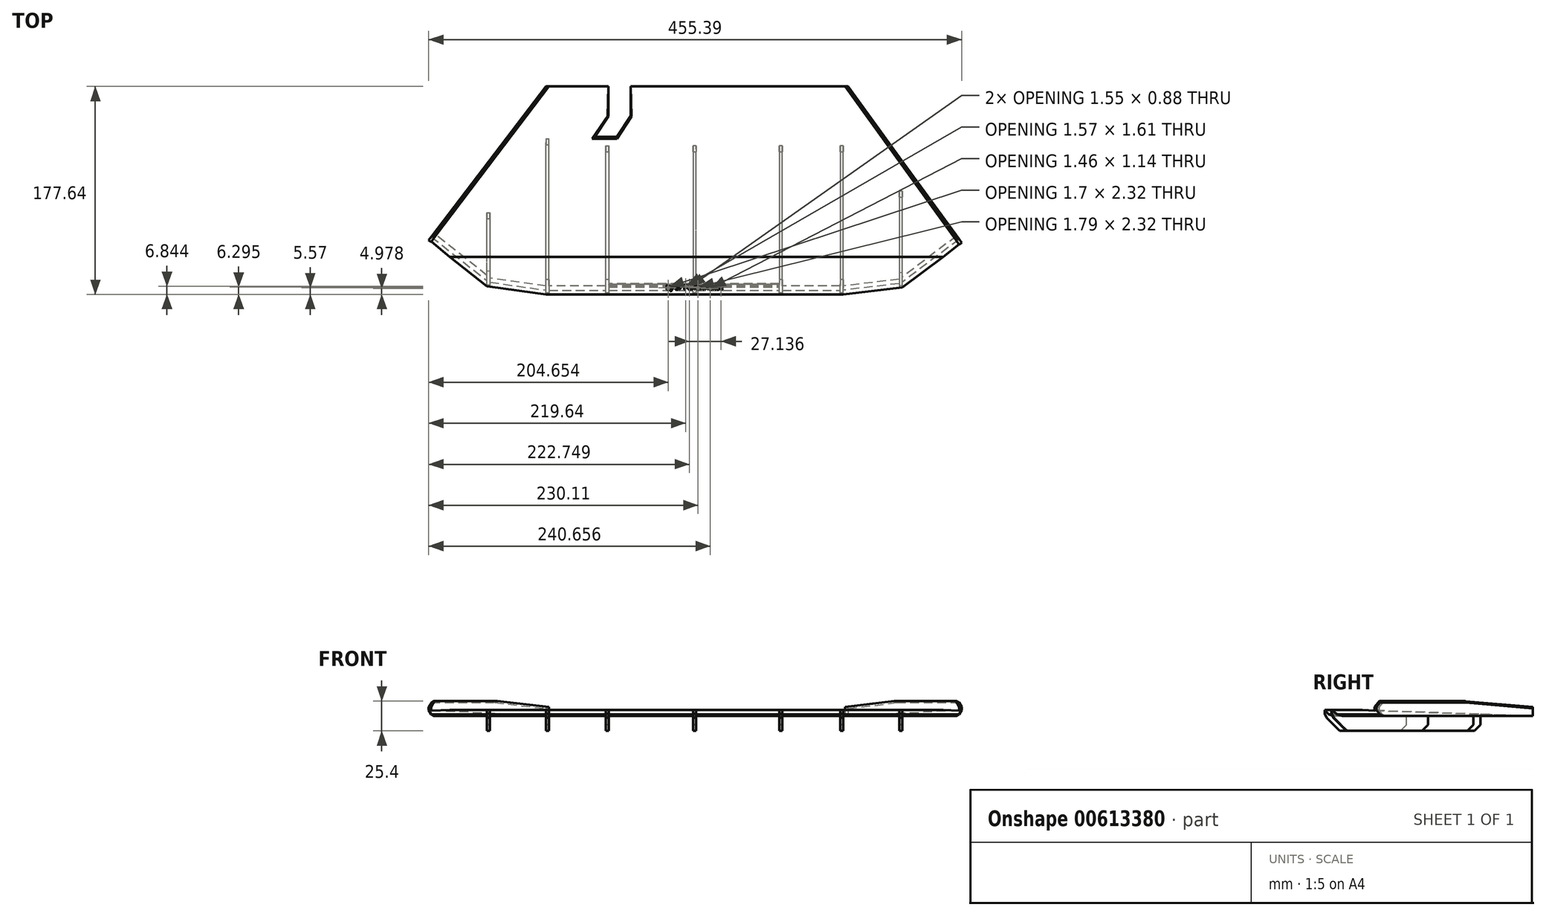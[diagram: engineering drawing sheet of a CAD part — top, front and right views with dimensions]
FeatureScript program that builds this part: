
annotation { "Feature Type Name" : "Feature", "Feature Type Description" : "" }
export const myFeature = defineFeature(function(context is Context, id is Id, definition is map)
    precondition{}
    {
        {
            var Q0;
            Q0=qCreatedBy(makeId("Top.planeOp"),FACE);
            var sketch = newSketch(context, id + "F0", { "sketchPlane" : qUnion([Q0])});
            skLineSegment(sketch, "E0.bottom", {"start": v(127, 146.68) * mm, "end": v(-127, 146.68) * mm});
            skLineSegment(sketch, "E0.top", {"start": v(127, 19.68) * mm, "end": v(-127, 19.68) * mm});
            skLineSegment(sketch, "E0.left", {"start": v(127, 146.68) * mm, "end": v(127, 19.68) * mm});
            skLineSegment(sketch, "E0.right", {"start": v(-127, 146.68) * mm, "end": v(-127, 19.68) * mm});
            skPoint(sketch, "E0.middle", {"position": v(0, 83.18) * mm});
            skLineSegment(sketch, "E1", {"start": v(-127, 146.68) * mm, "end": v(-127, 197.32) * mm});
            skLineSegment(sketch, "E2", {"start": v(-127, 197.32) * mm, "end": v(-73.7, 197.32) * mm});
            skLineSegment(sketch, "E3", {"start": v(-73.7, 197.32) * mm, "end": v(-73.7, 171.92) * mm});
            skLineSegment(sketch, "E4", {"start": v(-54.46, 171.92) * mm, "end": v(-54.46, 197.32) * mm});
            skLineSegment(sketch, "E5", {"start": v(-54.46, 197.32) * mm, "end": v(131.08, 197.32) * mm});
            skLineSegment(sketch, "E6", {"start": v(131.08, 197.32) * mm, "end": v(127, 146.68) * mm});
            skLineSegment(sketch, "E7", {"start": v(127, 19.68) * mm, "end": v(177.45, 25.67) * mm});
            skLineSegment(sketch, "E8", {"start": v(-127, 19.68) * mm, "end": v(-177.3, 26.78) * mm});
            skLineSegment(sketch, "E9", {"start": v(-177.3, 26.78) * mm, "end": v(-127, 197.32) * mm});
            skLineSegment(sketch, "E10", {"start": v(177.45, 25.67) * mm, "end": v(131.08, 197.32) * mm});
            skLineSegment(sketch, "E11", {"start": v(-73.7, 171.92) * mm, "end": v(-85.54, 154.36) * mm});
            skLineSegment(sketch, "E12", {"start": v(-85.54, 154.36) * mm, "end": v(-66.3, 154.36) * mm});
            skLineSegment(sketch, "E13", {"start": v(-66.3, 154.36) * mm, "end": v(-54.46, 171.92) * mm});
            skLineSegment(sketch, "E14", {"start": v(-177.3, 26.78) * mm, "end": v(-227.18, 66.08) * mm});
            skLineSegment(sketch, "E15", {"start": v(-227.18, 66.08) * mm, "end": v(-127, 197.32) * mm});
            skLineSegment(sketch, "E16", {"start": v(177.45, 25.67) * mm, "end": v(228.21, 63.82) * mm});
            skLineSegment(sketch, "E17", {"start": v(228.21, 63.82) * mm, "end": v(131.08, 197.32) * mm});
            skSolve(sketch);
        }
        {
            var Q0;
            Q0 = qSketchRegion(id + "F0", true);
            extrude(context, id + "F1", {"entities" : qUnion([Q0]), "depth" : 5.08 * mm, "offsetDistance" : 25.4 * mm});
        }
        {
            var Q0;
            Q0=makeQuery(id+"F1.opExtrude","CAP_FACE",FACE,{"disambiguationData":[OSD([sQuery(id+"F0.wireOp",EDGE,"E0.top"),sQuery(id+"F0.wireOp",EDGE,"E2"),sQuery(id+"F0.wireOp",EDGE,"E3"),sQuery(id+"F0.wireOp",EDGE,"E4"),sQuery(id+"F0.wireOp",EDGE,"E5"),sQuery(id+"F0.wireOp",EDGE,"E7"),sQuery(id+"F0.wireOp",EDGE,"E8"),sQuery(id+"F0.wireOp",EDGE,"E11"),sQuery(id+"F0.wireOp",EDGE,"E12"),sQuery(id+"F0.wireOp",EDGE,"E13"),sQuery(id+"F0.wireOp",EDGE,"E14"),sQuery(id+"F0.wireOp",EDGE,"E15"),sQuery(id+"F0.wireOp",EDGE,"E16"),sQuery(id+"F0.wireOp",EDGE,"E17")])],"isStart":false});
            var sketch = newSketch(context, id + "F2", { "sketchPlane" : qUnion([Q0])});
            skLineSegment(sketch, "E18", {"start": v(-227.18, 66.08) * mm, "end": v(-127, 197.32) * mm});
            skLineSegment(sketch, "E19", {"start": v(-227.18, 66.08) * mm, "end": v(-225.18, 64.51) * mm});
            skLineSegment(sketch, "E20", {"start": v(-124.46, 197.32) * mm, "end": v(-127, 197.32) * mm});
            skLineSegment(sketch, "E21", {"start": v(-225.18, 64.51) * mm, "end": v(-124.46, 197.32) * mm});
            skLineSegment(sketch, "E22", {"start": v(228.21, 63.82) * mm, "end": v(131.08, 197.32) * mm});
            skLineSegment(sketch, "E23", {"start": v(131.08, 197.32) * mm, "end": v(128.54, 197.32) * mm});
            skLineSegment(sketch, "E24", {"start": v(228.21, 63.82) * mm, "end": v(226.18, 62.29) * mm});
            skLineSegment(sketch, "E25", {"start": v(226.18, 62.29) * mm, "end": v(128.54, 197.32) * mm});
            skSolve(sketch);
        }
        {
            var Q0;
            Q0 = qSketchRegion(id + "F2", true);
            extrude(context, id + "F3", {"entities" : qUnion([Q0]), "operationType" : NewBodyOperationType.ADD, "depth" : 7.62 * mm, "offsetDistance" : 25.4 * mm});
        }
        {
            var Q0;
            Q0=makeQuery(id+"F1.opExtrude","CAP_FACE",FACE,{"disambiguationData":[OSD([sQuery(id+"F0.wireOp",EDGE,"E0.top"),sQuery(id+"F0.wireOp",EDGE,"E2"),sQuery(id+"F0.wireOp",EDGE,"E3"),sQuery(id+"F0.wireOp",EDGE,"E4"),sQuery(id+"F0.wireOp",EDGE,"E5"),sQuery(id+"F0.wireOp",EDGE,"E7"),sQuery(id+"F0.wireOp",EDGE,"E8"),sQuery(id+"F0.wireOp",EDGE,"E11"),sQuery(id+"F0.wireOp",EDGE,"E12"),sQuery(id+"F0.wireOp",EDGE,"E13"),sQuery(id+"F0.wireOp",EDGE,"E14"),sQuery(id+"F0.wireOp",EDGE,"E15"),sQuery(id+"F0.wireOp",EDGE,"E16"),sQuery(id+"F0.wireOp",EDGE,"E17")])],"isStart":true});
            var sketch = newSketch(context, id + "F4", { "sketchPlane" : qUnion([Q0])});
            skLineSegment(sketch, "E26", {"start": v(-127, -19.68) * mm, "end": v(-127, -152.72) * mm});
            skLineSegment(sketch, "E27", {"start": v(127, -19.68) * mm, "end": v(127, -146.68) * mm});
            skLineSegment(sketch, "E28", {"start": v(0, 0) * mm, "end": v(0, -146.68) * mm});
            skLineSegment(sketch, "E29", {"start": v(0, -146.68) * mm, "end": v(-1.27, -146.68) * mm});
            skLineSegment(sketch, "E30", {"start": v(0, -146.68) * mm, "end": v(1.27, -146.68) * mm});
            skLineSegment(sketch, "E31", {"start": v(-177.3, -26.78) * mm, "end": v(-177.3, -89.65) * mm});
            skLineSegment(sketch, "E32", {"start": v(177.45, -25.67) * mm, "end": v(177.45, -107.82) * mm});
            skLineSegment(sketch, "E33", {"start": v(-177.3, -26.78) * mm, "end": v(-174.79, -26.43) * mm});
            skLineSegment(sketch, "E34", {"start": v(-177.3, -89.65) * mm, "end": v(-174.76, -89.65) * mm});
            skLineSegment(sketch, "E35", {"start": v(-127, -19.68) * mm, "end": v(-124.46, -19.68) * mm});
            skLineSegment(sketch, "E36", {"start": v(-127, -152.72) * mm, "end": v(-124.46, -152.72) * mm});
            skLineSegment(sketch, "E37", {"start": v(0, -19.68) * mm, "end": v(-1.27, -19.68) * mm});
            skLineSegment(sketch, "E38", {"start": v(0, -19.68) * mm, "end": v(1.27, -19.68) * mm});
            skLineSegment(sketch, "E39", {"start": v(127, -19.68) * mm, "end": v(124.46, -19.68) * mm});
            skLineSegment(sketch, "E40", {"start": v(127, -146.68) * mm, "end": v(124.46, -146.68) * mm});
            skLineSegment(sketch, "E41", {"start": v(177.45, -25.67) * mm, "end": v(174.92, -25.37) * mm});
            skLineSegment(sketch, "E42", {"start": v(177.45, -107.82) * mm, "end": v(174.9, -107.82) * mm});
            skLineSegment(sketch, "E43", {"start": v(-174.76, -89.65) * mm, "end": v(-174.79, -26.43) * mm});
            skLineSegment(sketch, "E44", {"start": v(-124.46, -19.68) * mm, "end": v(-124.46, -152.72) * mm});
            skLineSegment(sketch, "E45", {"start": v(-1.27, -146.68) * mm, "end": v(-1.27, -19.68) * mm});
            skLineSegment(sketch, "E46", {"start": v(1.27, -19.68) * mm, "end": v(1.27, -146.68) * mm});
            skLineSegment(sketch, "E47", {"start": v(124.46, -146.68) * mm, "end": v(124.46, -19.68) * mm});
            skLineSegment(sketch, "E48", {"start": v(174.9, -107.82) * mm, "end": v(174.92, -25.37) * mm});
            skLineSegment(sketch, "E49", {"start": v(-75.92, -19.68) * mm, "end": v(-75.92, -146.68) * mm});
            skPoint(sketch, "E49.startSnap0", {"position": v(-75.92, -154.36) * mm});
            skLineSegment(sketch, "E50", {"start": v(74.96, -19.68) * mm, "end": v(74.96, -146.68) * mm});
            skLineSegment(sketch, "E51", {"start": v(74.96, -146.68) * mm, "end": v(72.42, -146.68) * mm});
            skLineSegment(sketch, "E52", {"start": v(74.96, -19.68) * mm, "end": v(72.42, -19.68) * mm});
            skLineSegment(sketch, "E53", {"start": v(-75.92, -19.68) * mm, "end": v(-73.38, -19.68) * mm});
            skLineSegment(sketch, "E54", {"start": v(-75.92, -146.68) * mm, "end": v(-73.38, -146.68) * mm});
            skLineSegment(sketch, "E55", {"start": v(-73.38, -146.68) * mm, "end": v(-73.38, -19.68) * mm});
            skLineSegment(sketch, "E56", {"start": v(72.42, -146.68) * mm, "end": v(72.42, -19.68) * mm});
            skSolve(sketch);
        }
        {
            var Q0;
            Q0 = qSketchRegion(id + "F4", true);
            extrude(context, id + "F5", {"entities" : qUnion([Q0]), "operationType" : NewBodyOperationType.ADD, "depth" : 12.7 * mm, "offsetDistance" : 25.4 * mm});
        }
        {
            var Q0;
            Q0=makeQuery(id+"F5.opExtrude","CAP_EDGE",EDGE,{"disambiguationData":[OSD([sQuery(id+"F4.wireOp",EDGE,"E33")])],"isStart":false});
            var Q1;
            Q1=makeQuery(id+"F5.opExtrude","CAP_EDGE",EDGE,{"disambiguationData":[OSD([sQuery(id+"F4.wireOp",EDGE,"E35")])],"isStart":false});
            var Q2;
            Q2=makeQuery(id+"F5.opExtrude","CAP_EDGE",EDGE,{"disambiguationData":[OSD([sQuery(id+"F4.wireOp",EDGE,"E53")])],"isStart":false});
            var Q3;
            Q3=makeQuery(id+"F5.opExtrude","CAP_EDGE",EDGE,{"disambiguationData":[OSD([sQuery(id+"F4.wireOp",EDGE,"E37"),sQuery(id+"F4.wireOp",EDGE,"E38")])],"isStart":false});
            var Q4;
            Q4=makeQuery(id+"F5.opExtrude","CAP_EDGE",EDGE,{"disambiguationData":[OSD([sQuery(id+"F4.wireOp",EDGE,"E52")])],"isStart":false});
            var Q5;
            Q5=makeQuery(id+"F5.opExtrude","CAP_EDGE",EDGE,{"disambiguationData":[OSD([sQuery(id+"F4.wireOp",EDGE,"E39")])],"isStart":false});
            var Q6;
            Q6=makeQuery(id+"F5.opExtrude","CAP_EDGE",EDGE,{"disambiguationData":[OSD([sQuery(id+"F4.wireOp",EDGE,"E41")])],"isStart":false});
            chamfer(context, id + "F6", {"entities" : qUnion([Q0, Q1, Q2, Q3, Q4, Q5, Q6]), "chamferType" : ChamferType.OFFSET_ANGLE, "width" : 12.7 * mm, "oppositeDirection" : false, "angle" : 45 * degree, "tangentPropagation" : true});
        }
        {
            var Q0;
            Q0=makeQuery(id+"F1.opExtrude","CAP_EDGE",EDGE,{"disambiguationData":[OSD([sQuery(id+"F0.wireOp",EDGE,"E14")])],"isStart":true});
            var Q1;
            Q1=makeQuery(id+"F1.opExtrude","CAP_EDGE",EDGE,{"disambiguationData":[OSD([sQuery(id+"F0.wireOp",EDGE,"E8")])],"isStart":true});
            var Q2;
            {var subQ0=sQuery(id+"F0.wireOp",EDGE,"E0.top");Q2=makeQuery(id+"F5.boolean.opBoolean","SPLIT",EDGE,{"disambiguationData":[TD([makeQuery(id+"F5.opExtrude","SWEPT_FACE",FACE,{"disambiguationData":[OSD([sQuery(id+"F4.wireOp",EDGE,"E44")])]})])],"derivedFrom":makeQuery(id+"F1.opExtrude","CAP_EDGE",EDGE,{"disambiguationData":[OSD([subQ0])],"isStart":true})});}
            var Q3;
            {var subQ0=sQuery(id+"F0.wireOp",EDGE,"E0.top");Q3=makeQuery(id+"F5.boolean.opBoolean","SPLIT",EDGE,{"disambiguationData":[TD([makeQuery(id+"F5.opExtrude","SWEPT_FACE",FACE,{"disambiguationData":[OSD([sQuery(id+"F4.wireOp",EDGE,"E45")])]})])],"derivedFrom":makeQuery(id+"F1.opExtrude","CAP_EDGE",EDGE,{"disambiguationData":[OSD([subQ0])],"isStart":true})});}
            var Q4;
            {var subQ0=sQuery(id+"F0.wireOp",EDGE,"E0.top");Q4=makeQuery(id+"F5.boolean.opBoolean","SPLIT",EDGE,{"disambiguationData":[TD([makeQuery(id+"F5.opExtrude","SWEPT_FACE",FACE,{"disambiguationData":[OSD([sQuery(id+"F4.wireOp",EDGE,"E46")])]})])],"derivedFrom":makeQuery(id+"F1.opExtrude","CAP_EDGE",EDGE,{"disambiguationData":[OSD([subQ0])],"isStart":true})});}
            var Q5;
            {var subQ0=sQuery(id+"F0.wireOp",EDGE,"E0.top");Q5=makeQuery(id+"F5.boolean.opBoolean","SPLIT",EDGE,{"disambiguationData":[TD([makeQuery(id+"F5.opExtrude","SWEPT_FACE",FACE,{"disambiguationData":[OSD([sQuery(id+"F4.wireOp",EDGE,"E47")])]})])],"derivedFrom":makeQuery(id+"F1.opExtrude","CAP_EDGE",EDGE,{"disambiguationData":[OSD([subQ0])],"isStart":true})});}
            var Q6;
            Q6=makeQuery(id+"F1.opExtrude","CAP_EDGE",EDGE,{"disambiguationData":[OSD([sQuery(id+"F0.wireOp",EDGE,"E7")])],"isStart":true});
            var Q7;
            Q7=makeQuery(id+"F1.opExtrude","CAP_EDGE",EDGE,{"disambiguationData":[OSD([sQuery(id+"F0.wireOp",EDGE,"E16")])],"isStart":true});
            chamfer(context, id + "F7", {"entities" : qUnion([Q0, Q1, Q2, Q3, Q4, Q5, Q6, Q7]), "width" : 5.08 * mm, "tangentPropagation" : true});
        }
        {
            var Q0;
            Q0=makeQuery(id+"F3.opExtrude","CAP_EDGE",EDGE,{"disambiguationData":[OSD([sQuery(id+"F2.wireOp",EDGE,"E23")])],"isStart":false});
            var Q1;
            Q1=makeQuery(id+"F3.opExtrude","CAP_EDGE",EDGE,{"disambiguationData":[OSD([sQuery(id+"F2.wireOp",EDGE,"E20")])],"isStart":false});
            chamfer(context, id + "F8", {"entities" : qUnion([Q0, Q1]), "chamferType" : ChamferType.OFFSET_ANGLE, "width" : 5.08 * mm, "oppositeDirection" : false, "angle" : 85 * degree, "tangentPropagation" : true});
        }
        {
            var Q0;
            Q0=makeQuery(id+"F3.opExtrude","CAP_EDGE",EDGE,{"disambiguationData":[OSD([sQuery(id+"F2.wireOp",EDGE,"E24")])],"isStart":false});
            var Q1;
            Q1=makeQuery(id+"F3.opExtrude","CAP_EDGE",EDGE,{"disambiguationData":[OSD([sQuery(id+"F2.wireOp",EDGE,"E19")])],"isStart":false});
            chamfer(context, id + "F9", {"entities" : qUnion([Q0, Q1]), "width" : 5.08 * mm, "tangentPropagation" : true});
        }
        {
            var Q0;
            {var subQ0=sQuery(id+"F4.wireOp",EDGE,"E53");Q0=makeQuery(id+"F6.opChamfer","BLEND_EDGE",EDGE,{"blendedFrom":[makeQuery(id+"F5.opExtrude","CAP_EDGE",EDGE,{"disambiguationData":[OSD([subQ0])],"isStart":false}),makeQuery(id+"F5.boolean.opBoolean","MERGE",FACE,{"derivedFrom":[makeQuery(id+"F1.opExtrude","SWEPT_FACE",FACE,{"disambiguationData":[OSD([sQuery(id+"F0.wireOp",EDGE,"E0.top")])]}),makeQuery(id+"F5.opExtrude","SWEPT_FACE",FACE,{"disambiguationData":[OSD([sQuery(id+"F4.wireOp",EDGE,"E35")])]}),makeQuery(id+"F5.opExtrude","SWEPT_FACE",FACE,{"disambiguationData":[OSD([sQuery(id+"F4.wireOp",EDGE,"E37"),sQuery(id+"F4.wireOp",EDGE,"E38")])]}),makeQuery(id+"F5.opExtrude","SWEPT_FACE",FACE,{"disambiguationData":[OSD([sQuery(id+"F4.wireOp",EDGE,"E39")])]}),makeQuery(id+"F5.opExtrude","SWEPT_FACE",FACE,{"disambiguationData":[OSD([sQuery(id+"F4.wireOp",EDGE,"E52")])]}),makeQuery(id+"F5.opExtrude","SWEPT_FACE",FACE,{"disambiguationData":[OSD([subQ0])]})]})],"blendedInto":[makeQuery(id+"F5.boolean.opBoolean","MERGE",FACE,{"derivedFrom":[makeQuery(id+"F1.opExtrude","SWEPT_FACE",FACE,{"disambiguationData":[OSD([sQuery(id+"F0.wireOp",EDGE,"E0.top")])]}),makeQuery(id+"F5.opExtrude","SWEPT_FACE",FACE,{"disambiguationData":[OSD([sQuery(id+"F4.wireOp",EDGE,"E35")])]}),makeQuery(id+"F5.opExtrude","SWEPT_FACE",FACE,{"disambiguationData":[OSD([sQuery(id+"F4.wireOp",EDGE,"E37"),sQuery(id+"F4.wireOp",EDGE,"E38")])]}),makeQuery(id+"F5.opExtrude","SWEPT_FACE",FACE,{"disambiguationData":[OSD([sQuery(id+"F4.wireOp",EDGE,"E39")])]}),makeQuery(id+"F5.opExtrude","SWEPT_FACE",FACE,{"disambiguationData":[OSD([sQuery(id+"F4.wireOp",EDGE,"E52")])]}),makeQuery(id+"F5.opExtrude","SWEPT_FACE",FACE,{"disambiguationData":[OSD([subQ0])]})]})]});}
            var Q1;
            {var subQ0=sQuery(id+"F4.wireOp",EDGE,"E38");var subQ1=sQuery(id+"F4.wireOp",EDGE,"E37");Q1=makeQuery(id+"F6.opChamfer","BLEND_EDGE",EDGE,{"blendedFrom":[makeQuery(id+"F5.opExtrude","CAP_EDGE",EDGE,{"disambiguationData":[OSD([subQ1,subQ0])],"isStart":false}),makeQuery(id+"F5.boolean.opBoolean","MERGE",FACE,{"derivedFrom":[makeQuery(id+"F1.opExtrude","SWEPT_FACE",FACE,{"disambiguationData":[OSD([sQuery(id+"F0.wireOp",EDGE,"E0.top")])]}),makeQuery(id+"F5.opExtrude","SWEPT_FACE",FACE,{"disambiguationData":[OSD([sQuery(id+"F4.wireOp",EDGE,"E35")])]}),makeQuery(id+"F5.opExtrude","SWEPT_FACE",FACE,{"disambiguationData":[OSD([subQ1,subQ0])]}),makeQuery(id+"F5.opExtrude","SWEPT_FACE",FACE,{"disambiguationData":[OSD([sQuery(id+"F4.wireOp",EDGE,"E39")])]}),makeQuery(id+"F5.opExtrude","SWEPT_FACE",FACE,{"disambiguationData":[OSD([sQuery(id+"F4.wireOp",EDGE,"E52")])]}),makeQuery(id+"F5.opExtrude","SWEPT_FACE",FACE,{"disambiguationData":[OSD([sQuery(id+"F4.wireOp",EDGE,"E53")])]})]})],"blendedInto":[makeQuery(id+"F5.boolean.opBoolean","MERGE",FACE,{"derivedFrom":[makeQuery(id+"F1.opExtrude","SWEPT_FACE",FACE,{"disambiguationData":[OSD([sQuery(id+"F0.wireOp",EDGE,"E0.top")])]}),makeQuery(id+"F5.opExtrude","SWEPT_FACE",FACE,{"disambiguationData":[OSD([sQuery(id+"F4.wireOp",EDGE,"E35")])]}),makeQuery(id+"F5.opExtrude","SWEPT_FACE",FACE,{"disambiguationData":[OSD([subQ1,subQ0])]}),makeQuery(id+"F5.opExtrude","SWEPT_FACE",FACE,{"disambiguationData":[OSD([sQuery(id+"F4.wireOp",EDGE,"E39")])]}),makeQuery(id+"F5.opExtrude","SWEPT_FACE",FACE,{"disambiguationData":[OSD([sQuery(id+"F4.wireOp",EDGE,"E52")])]}),makeQuery(id+"F5.opExtrude","SWEPT_FACE",FACE,{"disambiguationData":[OSD([sQuery(id+"F4.wireOp",EDGE,"E53")])]})]})]});}
            var Q2;
            {var subQ0=sQuery(id+"F4.wireOp",EDGE,"E52");Q2=makeQuery(id+"F6.opChamfer","BLEND_EDGE",EDGE,{"blendedFrom":[makeQuery(id+"F5.opExtrude","CAP_EDGE",EDGE,{"disambiguationData":[OSD([subQ0])],"isStart":false}),makeQuery(id+"F5.boolean.opBoolean","MERGE",FACE,{"derivedFrom":[makeQuery(id+"F1.opExtrude","SWEPT_FACE",FACE,{"disambiguationData":[OSD([sQuery(id+"F0.wireOp",EDGE,"E0.top")])]}),makeQuery(id+"F5.opExtrude","SWEPT_FACE",FACE,{"disambiguationData":[OSD([sQuery(id+"F4.wireOp",EDGE,"E35")])]}),makeQuery(id+"F5.opExtrude","SWEPT_FACE",FACE,{"disambiguationData":[OSD([sQuery(id+"F4.wireOp",EDGE,"E37"),sQuery(id+"F4.wireOp",EDGE,"E38")])]}),makeQuery(id+"F5.opExtrude","SWEPT_FACE",FACE,{"disambiguationData":[OSD([sQuery(id+"F4.wireOp",EDGE,"E39")])]}),makeQuery(id+"F5.opExtrude","SWEPT_FACE",FACE,{"disambiguationData":[OSD([subQ0])]}),makeQuery(id+"F5.opExtrude","SWEPT_FACE",FACE,{"disambiguationData":[OSD([sQuery(id+"F4.wireOp",EDGE,"E53")])]})]})],"blendedInto":[makeQuery(id+"F5.boolean.opBoolean","MERGE",FACE,{"derivedFrom":[makeQuery(id+"F1.opExtrude","SWEPT_FACE",FACE,{"disambiguationData":[OSD([sQuery(id+"F0.wireOp",EDGE,"E0.top")])]}),makeQuery(id+"F5.opExtrude","SWEPT_FACE",FACE,{"disambiguationData":[OSD([sQuery(id+"F4.wireOp",EDGE,"E35")])]}),makeQuery(id+"F5.opExtrude","SWEPT_FACE",FACE,{"disambiguationData":[OSD([sQuery(id+"F4.wireOp",EDGE,"E37"),sQuery(id+"F4.wireOp",EDGE,"E38")])]}),makeQuery(id+"F5.opExtrude","SWEPT_FACE",FACE,{"disambiguationData":[OSD([sQuery(id+"F4.wireOp",EDGE,"E39")])]}),makeQuery(id+"F5.opExtrude","SWEPT_FACE",FACE,{"disambiguationData":[OSD([subQ0])]}),makeQuery(id+"F5.opExtrude","SWEPT_FACE",FACE,{"disambiguationData":[OSD([sQuery(id+"F4.wireOp",EDGE,"E53")])]})]})]});}
            var Q3;
            {var subQ0=sQuery(id+"F4.wireOp",EDGE,"E39");Q3=makeQuery(id+"F6.opChamfer","BLEND_EDGE",EDGE,{"blendedFrom":[makeQuery(id+"F5.opExtrude","CAP_EDGE",EDGE,{"disambiguationData":[OSD([subQ0])],"isStart":false}),makeQuery(id+"F5.boolean.opBoolean","MERGE",FACE,{"derivedFrom":[makeQuery(id+"F1.opExtrude","SWEPT_FACE",FACE,{"disambiguationData":[OSD([sQuery(id+"F0.wireOp",EDGE,"E0.top")])]}),makeQuery(id+"F5.opExtrude","SWEPT_FACE",FACE,{"disambiguationData":[OSD([sQuery(id+"F4.wireOp",EDGE,"E35")])]}),makeQuery(id+"F5.opExtrude","SWEPT_FACE",FACE,{"disambiguationData":[OSD([sQuery(id+"F4.wireOp",EDGE,"E37"),sQuery(id+"F4.wireOp",EDGE,"E38")])]}),makeQuery(id+"F5.opExtrude","SWEPT_FACE",FACE,{"disambiguationData":[OSD([subQ0])]}),makeQuery(id+"F5.opExtrude","SWEPT_FACE",FACE,{"disambiguationData":[OSD([sQuery(id+"F4.wireOp",EDGE,"E52")])]}),makeQuery(id+"F5.opExtrude","SWEPT_FACE",FACE,{"disambiguationData":[OSD([sQuery(id+"F4.wireOp",EDGE,"E53")])]})]})],"blendedInto":[makeQuery(id+"F5.boolean.opBoolean","MERGE",FACE,{"derivedFrom":[makeQuery(id+"F1.opExtrude","SWEPT_FACE",FACE,{"disambiguationData":[OSD([sQuery(id+"F0.wireOp",EDGE,"E0.top")])]}),makeQuery(id+"F5.opExtrude","SWEPT_FACE",FACE,{"disambiguationData":[OSD([sQuery(id+"F4.wireOp",EDGE,"E35")])]}),makeQuery(id+"F5.opExtrude","SWEPT_FACE",FACE,{"disambiguationData":[OSD([sQuery(id+"F4.wireOp",EDGE,"E37"),sQuery(id+"F4.wireOp",EDGE,"E38")])]}),makeQuery(id+"F5.opExtrude","SWEPT_FACE",FACE,{"disambiguationData":[OSD([subQ0])]}),makeQuery(id+"F5.opExtrude","SWEPT_FACE",FACE,{"disambiguationData":[OSD([sQuery(id+"F4.wireOp",EDGE,"E52")])]}),makeQuery(id+"F5.opExtrude","SWEPT_FACE",FACE,{"disambiguationData":[OSD([sQuery(id+"F4.wireOp",EDGE,"E53")])]})]})]});}
            var Q4;
            {var subQ0=sQuery(id+"F4.wireOp",EDGE,"E41");Q4=makeQuery(id+"F6.opChamfer","BLEND_EDGE",EDGE,{"blendedFrom":[makeQuery(id+"F5.opExtrude","CAP_EDGE",EDGE,{"disambiguationData":[OSD([subQ0])],"isStart":false}),makeQuery(id+"F5.boolean.opBoolean","MERGE",FACE,{"derivedFrom":[makeQuery(id+"F1.opExtrude","SWEPT_FACE",FACE,{"disambiguationData":[OSD([sQuery(id+"F0.wireOp",EDGE,"E7")])]}),makeQuery(id+"F5.opExtrude","SWEPT_FACE",FACE,{"disambiguationData":[OSD([subQ0])]})]})],"blendedInto":[makeQuery(id+"F5.boolean.opBoolean","MERGE",FACE,{"derivedFrom":[makeQuery(id+"F1.opExtrude","SWEPT_FACE",FACE,{"disambiguationData":[OSD([sQuery(id+"F0.wireOp",EDGE,"E7")])]}),makeQuery(id+"F5.opExtrude","SWEPT_FACE",FACE,{"disambiguationData":[OSD([subQ0])]})]})]});}
            var Q5;
            {var subQ0=sQuery(id+"F4.wireOp",EDGE,"E33");Q5=makeQuery(id+"F6.opChamfer","BLEND_EDGE",EDGE,{"blendedFrom":[makeQuery(id+"F5.opExtrude","CAP_EDGE",EDGE,{"disambiguationData":[OSD([subQ0])],"isStart":false}),makeQuery(id+"F5.boolean.opBoolean","MERGE",FACE,{"derivedFrom":[makeQuery(id+"F1.opExtrude","SWEPT_FACE",FACE,{"disambiguationData":[OSD([sQuery(id+"F0.wireOp",EDGE,"E8")])]}),makeQuery(id+"F5.opExtrude","SWEPT_FACE",FACE,{"disambiguationData":[OSD([subQ0])]})]})],"blendedInto":[makeQuery(id+"F5.boolean.opBoolean","MERGE",FACE,{"derivedFrom":[makeQuery(id+"F1.opExtrude","SWEPT_FACE",FACE,{"disambiguationData":[OSD([sQuery(id+"F0.wireOp",EDGE,"E8")])]}),makeQuery(id+"F5.opExtrude","SWEPT_FACE",FACE,{"disambiguationData":[OSD([subQ0])]})]})]});}
            var Q6;
            {var subQ0=sQuery(id+"F4.wireOp",EDGE,"E35");Q6=makeQuery(id+"F6.opChamfer","BLEND_EDGE",EDGE,{"blendedFrom":[makeQuery(id+"F5.opExtrude","CAP_EDGE",EDGE,{"disambiguationData":[OSD([subQ0])],"isStart":false}),makeQuery(id+"F5.boolean.opBoolean","MERGE",FACE,{"derivedFrom":[makeQuery(id+"F1.opExtrude","SWEPT_FACE",FACE,{"disambiguationData":[OSD([sQuery(id+"F0.wireOp",EDGE,"E0.top")])]}),makeQuery(id+"F5.opExtrude","SWEPT_FACE",FACE,{"disambiguationData":[OSD([subQ0])]}),makeQuery(id+"F5.opExtrude","SWEPT_FACE",FACE,{"disambiguationData":[OSD([sQuery(id+"F4.wireOp",EDGE,"E37"),sQuery(id+"F4.wireOp",EDGE,"E38")])]}),makeQuery(id+"F5.opExtrude","SWEPT_FACE",FACE,{"disambiguationData":[OSD([sQuery(id+"F4.wireOp",EDGE,"E39")])]}),makeQuery(id+"F5.opExtrude","SWEPT_FACE",FACE,{"disambiguationData":[OSD([sQuery(id+"F4.wireOp",EDGE,"E52")])]}),makeQuery(id+"F5.opExtrude","SWEPT_FACE",FACE,{"disambiguationData":[OSD([sQuery(id+"F4.wireOp",EDGE,"E53")])]})]})],"blendedInto":[makeQuery(id+"F5.boolean.opBoolean","MERGE",FACE,{"derivedFrom":[makeQuery(id+"F1.opExtrude","SWEPT_FACE",FACE,{"disambiguationData":[OSD([sQuery(id+"F0.wireOp",EDGE,"E0.top")])]}),makeQuery(id+"F5.opExtrude","SWEPT_FACE",FACE,{"disambiguationData":[OSD([subQ0])]}),makeQuery(id+"F5.opExtrude","SWEPT_FACE",FACE,{"disambiguationData":[OSD([sQuery(id+"F4.wireOp",EDGE,"E37"),sQuery(id+"F4.wireOp",EDGE,"E38")])]}),makeQuery(id+"F5.opExtrude","SWEPT_FACE",FACE,{"disambiguationData":[OSD([sQuery(id+"F4.wireOp",EDGE,"E39")])]}),makeQuery(id+"F5.opExtrude","SWEPT_FACE",FACE,{"disambiguationData":[OSD([sQuery(id+"F4.wireOp",EDGE,"E52")])]}),makeQuery(id+"F5.opExtrude","SWEPT_FACE",FACE,{"disambiguationData":[OSD([sQuery(id+"F4.wireOp",EDGE,"E53")])]})]})]});}
            chamfer(context, id + "F10", {"entities" : qUnion([Q0, Q1, Q2, Q3, Q4, Q5, Q6]), "width" : 5.08 * mm, "tangentPropagation" : true});
        }
        {
            var Q0;
            {var subQ0=sQuery(id+"F0.wireOp",EDGE,"E0.top");var subQ1=makeQuery(id+"F1.opExtrude","CAP_FACE",FACE,{"disambiguationData":[OSD([subQ0,sQuery(id+"F0.wireOp",EDGE,"E2"),sQuery(id+"F0.wireOp",EDGE,"E3"),sQuery(id+"F0.wireOp",EDGE,"E4"),sQuery(id+"F0.wireOp",EDGE,"E5"),sQuery(id+"F0.wireOp",EDGE,"E7"),sQuery(id+"F0.wireOp",EDGE,"E8"),sQuery(id+"F0.wireOp",EDGE,"E11"),sQuery(id+"F0.wireOp",EDGE,"E12"),sQuery(id+"F0.wireOp",EDGE,"E13"),sQuery(id+"F0.wireOp",EDGE,"E14"),sQuery(id+"F0.wireOp",EDGE,"E15"),sQuery(id+"F0.wireOp",EDGE,"E16"),sQuery(id+"F0.wireOp",EDGE,"E17")])],"isStart":true});Q0=makeQuery(id+"F7.opChamfer","BLEND_EDGE",EDGE,{"blendedFrom":[makeQuery(id+"F5.boolean.opBoolean","SPLIT",EDGE,{"disambiguationData":[TD([makeQuery(id+"F5.opExtrude","SWEPT_FACE",FACE,{"disambiguationData":[OSD([sQuery(id+"F4.wireOp",EDGE,"E45")])]})])],"derivedFrom":makeQuery(id+"F1.opExtrude","CAP_EDGE",EDGE,{"disambiguationData":[OSD([subQ0])],"isStart":true})}),subQ1],"blendedInto":[subQ1]});}
            var Q1;
            {var subQ0=sQuery(id+"F0.wireOp",EDGE,"E0.top");var subQ1=makeQuery(id+"F1.opExtrude","CAP_FACE",FACE,{"disambiguationData":[OSD([subQ0,sQuery(id+"F0.wireOp",EDGE,"E2"),sQuery(id+"F0.wireOp",EDGE,"E3"),sQuery(id+"F0.wireOp",EDGE,"E4"),sQuery(id+"F0.wireOp",EDGE,"E5"),sQuery(id+"F0.wireOp",EDGE,"E7"),sQuery(id+"F0.wireOp",EDGE,"E8"),sQuery(id+"F0.wireOp",EDGE,"E11"),sQuery(id+"F0.wireOp",EDGE,"E12"),sQuery(id+"F0.wireOp",EDGE,"E13"),sQuery(id+"F0.wireOp",EDGE,"E14"),sQuery(id+"F0.wireOp",EDGE,"E15"),sQuery(id+"F0.wireOp",EDGE,"E16"),sQuery(id+"F0.wireOp",EDGE,"E17")])],"isStart":true});Q1=makeQuery(id+"F7.opChamfer","BLEND_EDGE",EDGE,{"blendedFrom":[makeQuery(id+"F5.boolean.opBoolean","SPLIT",EDGE,{"disambiguationData":[TD([makeQuery(id+"F5.opExtrude","SWEPT_FACE",FACE,{"disambiguationData":[OSD([sQuery(id+"F4.wireOp",EDGE,"E46")])]})])],"derivedFrom":makeQuery(id+"F1.opExtrude","CAP_EDGE",EDGE,{"disambiguationData":[OSD([subQ0])],"isStart":true})}),subQ1],"blendedInto":[subQ1]});}
            chamfer(context, id + "F11", {"entities" : qUnion([Q0, Q1]), "width" : 5.08 * mm, "tangentPropagation" : true});
        }
        {
            var Q0;
            {var subQ0=sQuery(id+"F0.wireOp",EDGE,"E0.top");var subQ1=makeQuery(id+"F1.opExtrude","CAP_FACE",FACE,{"disambiguationData":[OSD([subQ0,sQuery(id+"F0.wireOp",EDGE,"E2"),sQuery(id+"F0.wireOp",EDGE,"E3"),sQuery(id+"F0.wireOp",EDGE,"E4"),sQuery(id+"F0.wireOp",EDGE,"E5"),sQuery(id+"F0.wireOp",EDGE,"E7"),sQuery(id+"F0.wireOp",EDGE,"E8"),sQuery(id+"F0.wireOp",EDGE,"E11"),sQuery(id+"F0.wireOp",EDGE,"E12"),sQuery(id+"F0.wireOp",EDGE,"E13"),sQuery(id+"F0.wireOp",EDGE,"E14"),sQuery(id+"F0.wireOp",EDGE,"E15"),sQuery(id+"F0.wireOp",EDGE,"E16"),sQuery(id+"F0.wireOp",EDGE,"E17")])],"isStart":true});Q0=makeQuery(id+"F7.opChamfer","BLEND_EDGE",EDGE,{"blendedFrom":[makeQuery(id+"F5.boolean.opBoolean","SPLIT",EDGE,{"disambiguationData":[TD([makeQuery(id+"F5.opExtrude","SWEPT_FACE",FACE,{"disambiguationData":[OSD([sQuery(id+"F4.wireOp",EDGE,"E44")])]})])],"derivedFrom":makeQuery(id+"F1.opExtrude","CAP_EDGE",EDGE,{"disambiguationData":[OSD([subQ0])],"isStart":true})}),subQ1],"blendedInto":[subQ1]});}
            var Q1;
            {var subQ0=sQuery(id+"F0.wireOp",EDGE,"E8");Q1=makeQuery(id+"F7.opChamfer","BLEND_EDGE",EDGE,{"blendedFrom":[makeQuery(id+"F1.opExtrude","CAP_EDGE",EDGE,{"disambiguationData":[OSD([subQ0])],"isStart":true}),makeQuery(id+"F1.opExtrude","CAP_FACE",FACE,{"disambiguationData":[OSD([sQuery(id+"F0.wireOp",EDGE,"E0.top"),sQuery(id+"F0.wireOp",EDGE,"E2"),sQuery(id+"F0.wireOp",EDGE,"E3"),sQuery(id+"F0.wireOp",EDGE,"E4"),sQuery(id+"F0.wireOp",EDGE,"E5"),sQuery(id+"F0.wireOp",EDGE,"E7"),subQ0,sQuery(id+"F0.wireOp",EDGE,"E11"),sQuery(id+"F0.wireOp",EDGE,"E12"),sQuery(id+"F0.wireOp",EDGE,"E13"),sQuery(id+"F0.wireOp",EDGE,"E14"),sQuery(id+"F0.wireOp",EDGE,"E15"),sQuery(id+"F0.wireOp",EDGE,"E16"),sQuery(id+"F0.wireOp",EDGE,"E17")])],"isStart":true})],"blendedInto":[makeQuery(id+"F1.opExtrude","CAP_FACE",FACE,{"disambiguationData":[OSD([sQuery(id+"F0.wireOp",EDGE,"E0.top"),sQuery(id+"F0.wireOp",EDGE,"E2"),sQuery(id+"F0.wireOp",EDGE,"E3"),sQuery(id+"F0.wireOp",EDGE,"E4"),sQuery(id+"F0.wireOp",EDGE,"E5"),sQuery(id+"F0.wireOp",EDGE,"E7"),subQ0,sQuery(id+"F0.wireOp",EDGE,"E11"),sQuery(id+"F0.wireOp",EDGE,"E12"),sQuery(id+"F0.wireOp",EDGE,"E13"),sQuery(id+"F0.wireOp",EDGE,"E14"),sQuery(id+"F0.wireOp",EDGE,"E15"),sQuery(id+"F0.wireOp",EDGE,"E16"),sQuery(id+"F0.wireOp",EDGE,"E17")])],"isStart":true})]});}
            var Q2;
            {var subQ0=sQuery(id+"F0.wireOp",EDGE,"E14");Q2=makeQuery(id+"F7.opChamfer","BLEND_EDGE",EDGE,{"blendedFrom":[makeQuery(id+"F1.opExtrude","CAP_EDGE",EDGE,{"disambiguationData":[OSD([subQ0])],"isStart":true}),makeQuery(id+"F1.opExtrude","CAP_FACE",FACE,{"disambiguationData":[OSD([sQuery(id+"F0.wireOp",EDGE,"E0.top"),sQuery(id+"F0.wireOp",EDGE,"E2"),sQuery(id+"F0.wireOp",EDGE,"E3"),sQuery(id+"F0.wireOp",EDGE,"E4"),sQuery(id+"F0.wireOp",EDGE,"E5"),sQuery(id+"F0.wireOp",EDGE,"E7"),sQuery(id+"F0.wireOp",EDGE,"E8"),sQuery(id+"F0.wireOp",EDGE,"E11"),sQuery(id+"F0.wireOp",EDGE,"E12"),sQuery(id+"F0.wireOp",EDGE,"E13"),subQ0,sQuery(id+"F0.wireOp",EDGE,"E15"),sQuery(id+"F0.wireOp",EDGE,"E16"),sQuery(id+"F0.wireOp",EDGE,"E17")])],"isStart":true})],"blendedInto":[makeQuery(id+"F1.opExtrude","CAP_FACE",FACE,{"disambiguationData":[OSD([sQuery(id+"F0.wireOp",EDGE,"E0.top"),sQuery(id+"F0.wireOp",EDGE,"E2"),sQuery(id+"F0.wireOp",EDGE,"E3"),sQuery(id+"F0.wireOp",EDGE,"E4"),sQuery(id+"F0.wireOp",EDGE,"E5"),sQuery(id+"F0.wireOp",EDGE,"E7"),sQuery(id+"F0.wireOp",EDGE,"E8"),sQuery(id+"F0.wireOp",EDGE,"E11"),sQuery(id+"F0.wireOp",EDGE,"E12"),sQuery(id+"F0.wireOp",EDGE,"E13"),subQ0,sQuery(id+"F0.wireOp",EDGE,"E15"),sQuery(id+"F0.wireOp",EDGE,"E16"),sQuery(id+"F0.wireOp",EDGE,"E17")])],"isStart":true})]});}
            var Q3;
            {var subQ0=sQuery(id+"F0.wireOp",EDGE,"E0.top");var subQ1=makeQuery(id+"F1.opExtrude","CAP_FACE",FACE,{"disambiguationData":[OSD([subQ0,sQuery(id+"F0.wireOp",EDGE,"E2"),sQuery(id+"F0.wireOp",EDGE,"E3"),sQuery(id+"F0.wireOp",EDGE,"E4"),sQuery(id+"F0.wireOp",EDGE,"E5"),sQuery(id+"F0.wireOp",EDGE,"E7"),sQuery(id+"F0.wireOp",EDGE,"E8"),sQuery(id+"F0.wireOp",EDGE,"E11"),sQuery(id+"F0.wireOp",EDGE,"E12"),sQuery(id+"F0.wireOp",EDGE,"E13"),sQuery(id+"F0.wireOp",EDGE,"E14"),sQuery(id+"F0.wireOp",EDGE,"E15"),sQuery(id+"F0.wireOp",EDGE,"E16"),sQuery(id+"F0.wireOp",EDGE,"E17")])],"isStart":true});var subQ2=subQ1;Q3=makeQuery(id+"F11.opChamfer","BLEND_EDGE",EDGE,{"blendedFrom":[makeQuery(id+"F7.opChamfer","BLEND_EDGE",EDGE,{"blendedFrom":[makeQuery(id+"F5.boolean.opBoolean","SPLIT",EDGE,{"disambiguationData":[TD([makeQuery(id+"F5.opExtrude","SWEPT_FACE",FACE,{"disambiguationData":[OSD([sQuery(id+"F4.wireOp",EDGE,"E45")])]})])],"derivedFrom":makeQuery(id+"F1.opExtrude","CAP_EDGE",EDGE,{"disambiguationData":[OSD([subQ0])],"isStart":true})}),subQ2],"blendedInto":[subQ2]}),subQ2],"blendedInto":[subQ2]});}
            var Q4;
            {var subQ0=sQuery(id+"F0.wireOp",EDGE,"E0.top");var subQ1=makeQuery(id+"F1.opExtrude","CAP_FACE",FACE,{"disambiguationData":[OSD([subQ0,sQuery(id+"F0.wireOp",EDGE,"E2"),sQuery(id+"F0.wireOp",EDGE,"E3"),sQuery(id+"F0.wireOp",EDGE,"E4"),sQuery(id+"F0.wireOp",EDGE,"E5"),sQuery(id+"F0.wireOp",EDGE,"E7"),sQuery(id+"F0.wireOp",EDGE,"E8"),sQuery(id+"F0.wireOp",EDGE,"E11"),sQuery(id+"F0.wireOp",EDGE,"E12"),sQuery(id+"F0.wireOp",EDGE,"E13"),sQuery(id+"F0.wireOp",EDGE,"E14"),sQuery(id+"F0.wireOp",EDGE,"E15"),sQuery(id+"F0.wireOp",EDGE,"E16"),sQuery(id+"F0.wireOp",EDGE,"E17")])],"isStart":true});var subQ2=subQ1;Q4=makeQuery(id+"F11.opChamfer","BLEND_EDGE",EDGE,{"blendedFrom":[makeQuery(id+"F7.opChamfer","BLEND_EDGE",EDGE,{"blendedFrom":[makeQuery(id+"F5.boolean.opBoolean","SPLIT",EDGE,{"disambiguationData":[TD([makeQuery(id+"F5.opExtrude","SWEPT_FACE",FACE,{"disambiguationData":[OSD([sQuery(id+"F4.wireOp",EDGE,"E46")])]})])],"derivedFrom":makeQuery(id+"F1.opExtrude","CAP_EDGE",EDGE,{"disambiguationData":[OSD([subQ0])],"isStart":true})}),subQ2],"blendedInto":[subQ2]}),subQ2],"blendedInto":[subQ2]});}
            var Q5;
            {var subQ0=sQuery(id+"F0.wireOp",EDGE,"E0.top");var subQ1=makeQuery(id+"F1.opExtrude","CAP_FACE",FACE,{"disambiguationData":[OSD([subQ0,sQuery(id+"F0.wireOp",EDGE,"E2"),sQuery(id+"F0.wireOp",EDGE,"E3"),sQuery(id+"F0.wireOp",EDGE,"E4"),sQuery(id+"F0.wireOp",EDGE,"E5"),sQuery(id+"F0.wireOp",EDGE,"E7"),sQuery(id+"F0.wireOp",EDGE,"E8"),sQuery(id+"F0.wireOp",EDGE,"E11"),sQuery(id+"F0.wireOp",EDGE,"E12"),sQuery(id+"F0.wireOp",EDGE,"E13"),sQuery(id+"F0.wireOp",EDGE,"E14"),sQuery(id+"F0.wireOp",EDGE,"E15"),sQuery(id+"F0.wireOp",EDGE,"E16"),sQuery(id+"F0.wireOp",EDGE,"E17")])],"isStart":true});Q5=makeQuery(id+"F7.opChamfer","BLEND_EDGE",EDGE,{"blendedFrom":[makeQuery(id+"F5.boolean.opBoolean","SPLIT",EDGE,{"disambiguationData":[TD([makeQuery(id+"F5.opExtrude","SWEPT_FACE",FACE,{"disambiguationData":[OSD([sQuery(id+"F4.wireOp",EDGE,"E47")])]})])],"derivedFrom":makeQuery(id+"F1.opExtrude","CAP_EDGE",EDGE,{"disambiguationData":[OSD([subQ0])],"isStart":true})}),subQ1],"blendedInto":[subQ1]});}
            var Q6;
            {var subQ0=sQuery(id+"F0.wireOp",EDGE,"E7");Q6=makeQuery(id+"F7.opChamfer","BLEND_EDGE",EDGE,{"blendedFrom":[makeQuery(id+"F1.opExtrude","CAP_EDGE",EDGE,{"disambiguationData":[OSD([subQ0])],"isStart":true}),makeQuery(id+"F1.opExtrude","CAP_FACE",FACE,{"disambiguationData":[OSD([sQuery(id+"F0.wireOp",EDGE,"E0.top"),sQuery(id+"F0.wireOp",EDGE,"E2"),sQuery(id+"F0.wireOp",EDGE,"E3"),sQuery(id+"F0.wireOp",EDGE,"E4"),sQuery(id+"F0.wireOp",EDGE,"E5"),subQ0,sQuery(id+"F0.wireOp",EDGE,"E8"),sQuery(id+"F0.wireOp",EDGE,"E11"),sQuery(id+"F0.wireOp",EDGE,"E12"),sQuery(id+"F0.wireOp",EDGE,"E13"),sQuery(id+"F0.wireOp",EDGE,"E14"),sQuery(id+"F0.wireOp",EDGE,"E15"),sQuery(id+"F0.wireOp",EDGE,"E16"),sQuery(id+"F0.wireOp",EDGE,"E17")])],"isStart":true})],"blendedInto":[makeQuery(id+"F1.opExtrude","CAP_FACE",FACE,{"disambiguationData":[OSD([sQuery(id+"F0.wireOp",EDGE,"E0.top"),sQuery(id+"F0.wireOp",EDGE,"E2"),sQuery(id+"F0.wireOp",EDGE,"E3"),sQuery(id+"F0.wireOp",EDGE,"E4"),sQuery(id+"F0.wireOp",EDGE,"E5"),subQ0,sQuery(id+"F0.wireOp",EDGE,"E8"),sQuery(id+"F0.wireOp",EDGE,"E11"),sQuery(id+"F0.wireOp",EDGE,"E12"),sQuery(id+"F0.wireOp",EDGE,"E13"),sQuery(id+"F0.wireOp",EDGE,"E14"),sQuery(id+"F0.wireOp",EDGE,"E15"),sQuery(id+"F0.wireOp",EDGE,"E16"),sQuery(id+"F0.wireOp",EDGE,"E17")])],"isStart":true})]});}
            var Q7;
            {var subQ0=sQuery(id+"F0.wireOp",EDGE,"E16");Q7=makeQuery(id+"F7.opChamfer","BLEND_EDGE",EDGE,{"blendedFrom":[makeQuery(id+"F1.opExtrude","CAP_EDGE",EDGE,{"disambiguationData":[OSD([subQ0])],"isStart":true}),makeQuery(id+"F1.opExtrude","CAP_FACE",FACE,{"disambiguationData":[OSD([sQuery(id+"F0.wireOp",EDGE,"E0.top"),sQuery(id+"F0.wireOp",EDGE,"E2"),sQuery(id+"F0.wireOp",EDGE,"E3"),sQuery(id+"F0.wireOp",EDGE,"E4"),sQuery(id+"F0.wireOp",EDGE,"E5"),sQuery(id+"F0.wireOp",EDGE,"E7"),sQuery(id+"F0.wireOp",EDGE,"E8"),sQuery(id+"F0.wireOp",EDGE,"E11"),sQuery(id+"F0.wireOp",EDGE,"E12"),sQuery(id+"F0.wireOp",EDGE,"E13"),sQuery(id+"F0.wireOp",EDGE,"E14"),sQuery(id+"F0.wireOp",EDGE,"E15"),subQ0,sQuery(id+"F0.wireOp",EDGE,"E17")])],"isStart":true})],"blendedInto":[makeQuery(id+"F1.opExtrude","CAP_FACE",FACE,{"disambiguationData":[OSD([sQuery(id+"F0.wireOp",EDGE,"E0.top"),sQuery(id+"F0.wireOp",EDGE,"E2"),sQuery(id+"F0.wireOp",EDGE,"E3"),sQuery(id+"F0.wireOp",EDGE,"E4"),sQuery(id+"F0.wireOp",EDGE,"E5"),sQuery(id+"F0.wireOp",EDGE,"E7"),sQuery(id+"F0.wireOp",EDGE,"E8"),sQuery(id+"F0.wireOp",EDGE,"E11"),sQuery(id+"F0.wireOp",EDGE,"E12"),sQuery(id+"F0.wireOp",EDGE,"E13"),sQuery(id+"F0.wireOp",EDGE,"E14"),sQuery(id+"F0.wireOp",EDGE,"E15"),subQ0,sQuery(id+"F0.wireOp",EDGE,"E17")])],"isStart":true})]});}
            chamfer(context, id + "F12", {"entities" : qUnion([Q0, Q1, Q2, Q3, Q4, Q5, Q6, Q7]), "width" : 5.08 * mm, "tangentPropagation" : true});
        }
        {
            var Q0;
            Q0=makeQuery(id+"F1.opExtrude","CAP_FACE",FACE,{"disambiguationData":[OSD([sQuery(id+"F0.wireOp",EDGE,"E0.top"),sQuery(id+"F0.wireOp",EDGE,"E2"),sQuery(id+"F0.wireOp",EDGE,"E3"),sQuery(id+"F0.wireOp",EDGE,"E4"),sQuery(id+"F0.wireOp",EDGE,"E5"),sQuery(id+"F0.wireOp",EDGE,"E7"),sQuery(id+"F0.wireOp",EDGE,"E8"),sQuery(id+"F0.wireOp",EDGE,"E11"),sQuery(id+"F0.wireOp",EDGE,"E12"),sQuery(id+"F0.wireOp",EDGE,"E13"),sQuery(id+"F0.wireOp",EDGE,"E14"),sQuery(id+"F0.wireOp",EDGE,"E15"),sQuery(id+"F0.wireOp",EDGE,"E16"),sQuery(id+"F0.wireOp",EDGE,"E17")])],"isStart":false});
            var sketch = newSketch(context, id + "F13", { "sketchPlane" : qUnion([Q0])});
            skText(sketch, "E57", { "text": "by SF Performance", "fontName": "OpenSans-Regular.ttf"});
            const initialGuessF13  = {"E57": [-0.0243, 0.02377, 1, 0, 0.00399]};
            skSetInitialGuess(sketch, initialGuessF13);
            skSolve(sketch);
        }
        {
            var Q0;
            Q0 = qSketchRegion(id + "F13", true);
            extrude(context, id + "F14", {"entities" : qUnion([Q0]), "depth" : 0.03 * mm, "offsetDistance" : 25.4 * mm});
        }
        {
            var Q0;
            Q0=makeQuery(id+"F1.opExtrude","CAP_EDGE",EDGE,{"disambiguationData":[OSD([sQuery(id+"F0.wireOp",EDGE,"E12")])],"isStart":false});
            chamfer(context, id + "F15", {"entities" : qUnion([Q0]), "width" : 5.08 * mm, "tangentPropagation" : true});
        }
        {
            var Q0;
            Q0=makeQuery(id+"F1.opExtrude","CAP_EDGE",EDGE,{"disambiguationData":[OSD([sQuery(id+"F0.wireOp",EDGE,"E13")])],"isStart":false});
            var Q1;
            Q1=makeQuery(id+"F1.opExtrude","CAP_EDGE",EDGE,{"disambiguationData":[OSD([sQuery(id+"F0.wireOp",EDGE,"E4")])],"isStart":false});
            var Q2;
            Q2=makeQuery(id+"F1.opExtrude","CAP_EDGE",EDGE,{"disambiguationData":[OSD([sQuery(id+"F0.wireOp",EDGE,"E3")])],"isStart":false});
            var Q3;
            Q3=makeQuery(id+"F1.opExtrude","CAP_EDGE",EDGE,{"disambiguationData":[OSD([sQuery(id+"F0.wireOp",EDGE,"E11")])],"isStart":false});
            chamfer(context, id + "F16", {"entities" : qUnion([Q0, Q1, Q2, Q3]), "chamferType" : ChamferType.OFFSET_ANGLE, "width" : 5.08 * mm, "oppositeDirection" : false, "angle" : 30 * degree, "tangentPropagation" : true});
        }
        {
            var Q0;
            Q0=makeQuery(id+"F5.opExtrude","CAP_EDGE",EDGE,{"disambiguationData":[OSD([sQuery(id+"F4.wireOp",EDGE,"E34")])],"isStart":false});
            var Q1;
            Q1=makeQuery(id+"F5.opExtrude","CAP_EDGE",EDGE,{"disambiguationData":[OSD([sQuery(id+"F4.wireOp",EDGE,"E36")])],"isStart":false});
            var Q2;
            Q2=makeQuery(id+"F5.opExtrude","CAP_EDGE",EDGE,{"disambiguationData":[OSD([sQuery(id+"F4.wireOp",EDGE,"E54")])],"isStart":false});
            var Q3;
            Q3=makeQuery(id+"F5.opExtrude","CAP_EDGE",EDGE,{"disambiguationData":[OSD([sQuery(id+"F4.wireOp",EDGE,"E29"),sQuery(id+"F4.wireOp",EDGE,"E30")])],"isStart":false});
            var Q4;
            Q4=makeQuery(id+"F5.opExtrude","CAP_EDGE",EDGE,{"disambiguationData":[OSD([sQuery(id+"F4.wireOp",EDGE,"E51")])],"isStart":false});
            var Q5;
            Q5=makeQuery(id+"F5.opExtrude","CAP_EDGE",EDGE,{"disambiguationData":[OSD([sQuery(id+"F4.wireOp",EDGE,"E40")])],"isStart":false});
            var Q6;
            Q6=makeQuery(id+"F5.opExtrude","CAP_EDGE",EDGE,{"disambiguationData":[OSD([sQuery(id+"F4.wireOp",EDGE,"E42")])],"isStart":false});
            chamfer(context, id + "F17", {"entities" : qUnion([Q0, Q1, Q2, Q3, Q4, Q5, Q6]), "width" : 5.08 * mm, "tangentPropagation" : true});
        }
        {
            var Q0;
            Q0=makeQuery(id+"F1.opExtrude","CAP_EDGE",EDGE,{"disambiguationData":[OSD([sQuery(id+"F0.wireOp",EDGE,"E5")])],"isStart":false});
            chamfer(context, id + "F18", {"entities" : qUnion([Q0]), "chamferType" : ChamferType.OFFSET_ANGLE, "width" : 5.08 * mm, "oppositeDirection" : false, "angle" : 88 * degree, "tangentPropagation" : true});
        }
        {
            var Q0;
            Q0=makeQuery(id+"F3.opExtrude","CAP_EDGE",EDGE,{"disambiguationData":[OSD([sQuery(id+"F2.wireOp",EDGE,"E18")])],"isStart":false});
            var Q1;
            Q1=makeQuery(id+"F8.opChamfer","BLEND_EDGE",EDGE,{"blendedFrom":[makeQuery(id+"F3.opExtrude","CAP_EDGE",EDGE,{"disambiguationData":[OSD([sQuery(id+"F2.wireOp",EDGE,"E20")])],"isStart":false}),makeQuery(id+"F3.boolean.opBoolean","MERGE",FACE,{"derivedFrom":[makeQuery(id+"F1.opExtrude","SWEPT_FACE",FACE,{"disambiguationData":[OSD([sQuery(id+"F0.wireOp",EDGE,"E15")])]}),makeQuery(id+"F3.opExtrude","SWEPT_FACE",FACE,{"disambiguationData":[OSD([sQuery(id+"F2.wireOp",EDGE,"E18")])]})]})],"blendedInto":[makeQuery(id+"F3.boolean.opBoolean","MERGE",FACE,{"derivedFrom":[makeQuery(id+"F1.opExtrude","SWEPT_FACE",FACE,{"disambiguationData":[OSD([sQuery(id+"F0.wireOp",EDGE,"E15")])]}),makeQuery(id+"F3.opExtrude","SWEPT_FACE",FACE,{"disambiguationData":[OSD([sQuery(id+"F2.wireOp",EDGE,"E18")])]})]})]});
            var Q2;
            Q2=makeQuery(id+"F3.opExtrude","CAP_EDGE",EDGE,{"disambiguationData":[OSD([sQuery(id+"F2.wireOp",EDGE,"E22")])],"isStart":false});
            var Q3;
            Q3=makeQuery(id+"F8.opChamfer","BLEND_EDGE",EDGE,{"blendedFrom":[makeQuery(id+"F3.opExtrude","CAP_EDGE",EDGE,{"disambiguationData":[OSD([sQuery(id+"F2.wireOp",EDGE,"E23")])],"isStart":false}),makeQuery(id+"F3.boolean.opBoolean","MERGE",FACE,{"derivedFrom":[makeQuery(id+"F1.opExtrude","SWEPT_FACE",FACE,{"disambiguationData":[OSD([sQuery(id+"F0.wireOp",EDGE,"E17")])]}),makeQuery(id+"F3.opExtrude","SWEPT_FACE",FACE,{"disambiguationData":[OSD([sQuery(id+"F2.wireOp",EDGE,"E22")])]})]})],"blendedInto":[makeQuery(id+"F3.boolean.opBoolean","MERGE",FACE,{"derivedFrom":[makeQuery(id+"F1.opExtrude","SWEPT_FACE",FACE,{"disambiguationData":[OSD([sQuery(id+"F0.wireOp",EDGE,"E17")])]}),makeQuery(id+"F3.opExtrude","SWEPT_FACE",FACE,{"disambiguationData":[OSD([sQuery(id+"F2.wireOp",EDGE,"E22")])]})]})]});
            chamfer(context, id + "F19", {"entities" : qUnion([Q0, Q1, Q2, Q3]), "width" : 1.27 * mm, "tangentPropagation" : true});
        }
        {
            var Q0;
            {var subQ0=sQuery(id+"F0.wireOp",EDGE,"E0.top");var subQ1=makeQuery(id+"F1.opExtrude","CAP_FACE",FACE,{"disambiguationData":[OSD([subQ0,sQuery(id+"F0.wireOp",EDGE,"E2"),sQuery(id+"F0.wireOp",EDGE,"E3"),sQuery(id+"F0.wireOp",EDGE,"E4"),sQuery(id+"F0.wireOp",EDGE,"E5"),sQuery(id+"F0.wireOp",EDGE,"E7"),sQuery(id+"F0.wireOp",EDGE,"E8"),sQuery(id+"F0.wireOp",EDGE,"E11"),sQuery(id+"F0.wireOp",EDGE,"E12"),sQuery(id+"F0.wireOp",EDGE,"E13"),sQuery(id+"F0.wireOp",EDGE,"E14"),sQuery(id+"F0.wireOp",EDGE,"E15"),sQuery(id+"F0.wireOp",EDGE,"E16"),sQuery(id+"F0.wireOp",EDGE,"E17")])],"isStart":true});var subQ2=subQ1;var subQ3=subQ2;Q0=makeQuery(id+"F12.opChamfer","BLEND_EDGE",EDGE,{"blendedFrom":[makeQuery(id+"F11.opChamfer","BLEND_EDGE",EDGE,{"blendedFrom":[makeQuery(id+"F7.opChamfer","BLEND_EDGE",EDGE,{"blendedFrom":[makeQuery(id+"F5.boolean.opBoolean","SPLIT",EDGE,{"disambiguationData":[TD([makeQuery(id+"F5.opExtrude","SWEPT_FACE",FACE,{"disambiguationData":[OSD([sQuery(id+"F4.wireOp",EDGE,"E45")])]})])],"derivedFrom":makeQuery(id+"F1.opExtrude","CAP_EDGE",EDGE,{"disambiguationData":[OSD([subQ0])],"isStart":true})}),subQ2],"blendedInto":[subQ2]}),subQ3],"blendedInto":[subQ3]}),subQ3],"blendedInto":[subQ3]});}
            var Q1;
            {var subQ0=sQuery(id+"F0.wireOp",EDGE,"E0.top");var subQ1=makeQuery(id+"F1.opExtrude","CAP_FACE",FACE,{"disambiguationData":[OSD([subQ0,sQuery(id+"F0.wireOp",EDGE,"E2"),sQuery(id+"F0.wireOp",EDGE,"E3"),sQuery(id+"F0.wireOp",EDGE,"E4"),sQuery(id+"F0.wireOp",EDGE,"E5"),sQuery(id+"F0.wireOp",EDGE,"E7"),sQuery(id+"F0.wireOp",EDGE,"E8"),sQuery(id+"F0.wireOp",EDGE,"E11"),sQuery(id+"F0.wireOp",EDGE,"E12"),sQuery(id+"F0.wireOp",EDGE,"E13"),sQuery(id+"F0.wireOp",EDGE,"E14"),sQuery(id+"F0.wireOp",EDGE,"E15"),sQuery(id+"F0.wireOp",EDGE,"E16"),sQuery(id+"F0.wireOp",EDGE,"E17")])],"isStart":true});var subQ2=subQ1;var subQ3=subQ2;Q1=makeQuery(id+"F12.opChamfer","BLEND_EDGE",EDGE,{"blendedFrom":[makeQuery(id+"F11.opChamfer","BLEND_EDGE",EDGE,{"blendedFrom":[makeQuery(id+"F7.opChamfer","BLEND_EDGE",EDGE,{"blendedFrom":[makeQuery(id+"F5.boolean.opBoolean","SPLIT",EDGE,{"disambiguationData":[TD([makeQuery(id+"F5.opExtrude","SWEPT_FACE",FACE,{"disambiguationData":[OSD([sQuery(id+"F4.wireOp",EDGE,"E46")])]})])],"derivedFrom":makeQuery(id+"F1.opExtrude","CAP_EDGE",EDGE,{"disambiguationData":[OSD([subQ0])],"isStart":true})}),subQ2],"blendedInto":[subQ2]}),subQ3],"blendedInto":[subQ3]}),subQ3],"blendedInto":[subQ3]});}
            chamfer(context, id + "F20", {"entities" : qUnion([Q0, Q1]), "width" : 5.08 * mm, "tangentPropagation" : true});
        }
        {
            var Q0;
            {var subQ0=sQuery(id+"F0.wireOp",EDGE,"E0.top");var subQ1=makeQuery(id+"F1.opExtrude","CAP_FACE",FACE,{"disambiguationData":[OSD([subQ0,sQuery(id+"F0.wireOp",EDGE,"E2"),sQuery(id+"F0.wireOp",EDGE,"E3"),sQuery(id+"F0.wireOp",EDGE,"E4"),sQuery(id+"F0.wireOp",EDGE,"E5"),sQuery(id+"F0.wireOp",EDGE,"E7"),sQuery(id+"F0.wireOp",EDGE,"E8"),sQuery(id+"F0.wireOp",EDGE,"E11"),sQuery(id+"F0.wireOp",EDGE,"E12"),sQuery(id+"F0.wireOp",EDGE,"E13"),sQuery(id+"F0.wireOp",EDGE,"E14"),sQuery(id+"F0.wireOp",EDGE,"E15"),sQuery(id+"F0.wireOp",EDGE,"E16"),sQuery(id+"F0.wireOp",EDGE,"E17")])],"isStart":true});var subQ2=subQ1;var subQ3=subQ2;var subQ4=subQ3;Q0=makeQuery(id+"F20.opChamfer","BLEND_EDGE",EDGE,{"blendedFrom":[makeQuery(id+"F12.opChamfer","BLEND_EDGE",EDGE,{"blendedFrom":[makeQuery(id+"F11.opChamfer","BLEND_EDGE",EDGE,{"blendedFrom":[makeQuery(id+"F7.opChamfer","BLEND_EDGE",EDGE,{"blendedFrom":[makeQuery(id+"F5.boolean.opBoolean","SPLIT",EDGE,{"disambiguationData":[TD([makeQuery(id+"F5.opExtrude","SWEPT_FACE",FACE,{"disambiguationData":[OSD([sQuery(id+"F4.wireOp",EDGE,"E45")])]})])],"derivedFrom":makeQuery(id+"F1.opExtrude","CAP_EDGE",EDGE,{"disambiguationData":[OSD([subQ0])],"isStart":true})}),subQ2],"blendedInto":[subQ2]}),subQ3],"blendedInto":[subQ3]}),subQ4],"blendedInto":[subQ4]}),subQ4],"blendedInto":[subQ4]});}
            var Q1;
            {var subQ0=sQuery(id+"F0.wireOp",EDGE,"E0.top");var subQ1=makeQuery(id+"F1.opExtrude","CAP_FACE",FACE,{"disambiguationData":[OSD([subQ0,sQuery(id+"F0.wireOp",EDGE,"E2"),sQuery(id+"F0.wireOp",EDGE,"E3"),sQuery(id+"F0.wireOp",EDGE,"E4"),sQuery(id+"F0.wireOp",EDGE,"E5"),sQuery(id+"F0.wireOp",EDGE,"E7"),sQuery(id+"F0.wireOp",EDGE,"E8"),sQuery(id+"F0.wireOp",EDGE,"E11"),sQuery(id+"F0.wireOp",EDGE,"E12"),sQuery(id+"F0.wireOp",EDGE,"E13"),sQuery(id+"F0.wireOp",EDGE,"E14"),sQuery(id+"F0.wireOp",EDGE,"E15"),sQuery(id+"F0.wireOp",EDGE,"E16"),sQuery(id+"F0.wireOp",EDGE,"E17")])],"isStart":true});var subQ2=subQ1;var subQ3=subQ2;var subQ4=subQ3;Q1=makeQuery(id+"F20.opChamfer","BLEND_EDGE",EDGE,{"blendedFrom":[makeQuery(id+"F12.opChamfer","BLEND_EDGE",EDGE,{"blendedFrom":[makeQuery(id+"F11.opChamfer","BLEND_EDGE",EDGE,{"blendedFrom":[makeQuery(id+"F7.opChamfer","BLEND_EDGE",EDGE,{"blendedFrom":[makeQuery(id+"F5.boolean.opBoolean","SPLIT",EDGE,{"disambiguationData":[TD([makeQuery(id+"F5.opExtrude","SWEPT_FACE",FACE,{"disambiguationData":[OSD([sQuery(id+"F4.wireOp",EDGE,"E46")])]})])],"derivedFrom":makeQuery(id+"F1.opExtrude","CAP_EDGE",EDGE,{"disambiguationData":[OSD([subQ0])],"isStart":true})}),subQ2],"blendedInto":[subQ2]}),subQ3],"blendedInto":[subQ3]}),subQ4],"blendedInto":[subQ4]}),subQ4],"blendedInto":[subQ4]});}
            chamfer(context, id + "F21", {"entities" : qUnion([Q0, Q1]), "width" : 5.08 * mm, "tangentPropagation" : true});
        }
        {
            var Q0;
            {var subQ0=sQuery(id+"F0.wireOp",EDGE,"E0.top");var subQ1=makeQuery(id+"F1.opExtrude","CAP_FACE",FACE,{"disambiguationData":[OSD([subQ0,sQuery(id+"F0.wireOp",EDGE,"E2"),sQuery(id+"F0.wireOp",EDGE,"E3"),sQuery(id+"F0.wireOp",EDGE,"E4"),sQuery(id+"F0.wireOp",EDGE,"E5"),sQuery(id+"F0.wireOp",EDGE,"E7"),sQuery(id+"F0.wireOp",EDGE,"E8"),sQuery(id+"F0.wireOp",EDGE,"E11"),sQuery(id+"F0.wireOp",EDGE,"E12"),sQuery(id+"F0.wireOp",EDGE,"E13"),sQuery(id+"F0.wireOp",EDGE,"E14"),sQuery(id+"F0.wireOp",EDGE,"E15"),sQuery(id+"F0.wireOp",EDGE,"E16"),sQuery(id+"F0.wireOp",EDGE,"E17")])],"isStart":true});var subQ2=subQ1;var subQ3=subQ2;var subQ4=subQ3;var subQ5=subQ4;Q0=makeQuery(id+"F21.opChamfer","BLEND_EDGE",EDGE,{"blendedFrom":[makeQuery(id+"F20.opChamfer","BLEND_EDGE",EDGE,{"blendedFrom":[makeQuery(id+"F12.opChamfer","BLEND_EDGE",EDGE,{"blendedFrom":[makeQuery(id+"F11.opChamfer","BLEND_EDGE",EDGE,{"blendedFrom":[makeQuery(id+"F7.opChamfer","BLEND_EDGE",EDGE,{"blendedFrom":[makeQuery(id+"F5.boolean.opBoolean","SPLIT",EDGE,{"disambiguationData":[TD([makeQuery(id+"F5.opExtrude","SWEPT_FACE",FACE,{"disambiguationData":[OSD([sQuery(id+"F4.wireOp",EDGE,"E45")])]})])],"derivedFrom":makeQuery(id+"F1.opExtrude","CAP_EDGE",EDGE,{"disambiguationData":[OSD([subQ0])],"isStart":true})}),subQ2],"blendedInto":[subQ2]}),subQ3],"blendedInto":[subQ3]}),subQ4],"blendedInto":[subQ4]}),subQ5],"blendedInto":[subQ5]}),subQ5],"blendedInto":[subQ5]});}
            var Q1;
            {var subQ0=sQuery(id+"F0.wireOp",EDGE,"E0.top");var subQ1=makeQuery(id+"F1.opExtrude","CAP_FACE",FACE,{"disambiguationData":[OSD([subQ0,sQuery(id+"F0.wireOp",EDGE,"E2"),sQuery(id+"F0.wireOp",EDGE,"E3"),sQuery(id+"F0.wireOp",EDGE,"E4"),sQuery(id+"F0.wireOp",EDGE,"E5"),sQuery(id+"F0.wireOp",EDGE,"E7"),sQuery(id+"F0.wireOp",EDGE,"E8"),sQuery(id+"F0.wireOp",EDGE,"E11"),sQuery(id+"F0.wireOp",EDGE,"E12"),sQuery(id+"F0.wireOp",EDGE,"E13"),sQuery(id+"F0.wireOp",EDGE,"E14"),sQuery(id+"F0.wireOp",EDGE,"E15"),sQuery(id+"F0.wireOp",EDGE,"E16"),sQuery(id+"F0.wireOp",EDGE,"E17")])],"isStart":true});var subQ2=subQ1;var subQ3=subQ2;var subQ4=subQ3;var subQ5=subQ4;Q1=makeQuery(id+"F21.opChamfer","BLEND_EDGE",EDGE,{"blendedFrom":[makeQuery(id+"F20.opChamfer","BLEND_EDGE",EDGE,{"blendedFrom":[makeQuery(id+"F12.opChamfer","BLEND_EDGE",EDGE,{"blendedFrom":[makeQuery(id+"F11.opChamfer","BLEND_EDGE",EDGE,{"blendedFrom":[makeQuery(id+"F7.opChamfer","BLEND_EDGE",EDGE,{"blendedFrom":[makeQuery(id+"F5.boolean.opBoolean","SPLIT",EDGE,{"disambiguationData":[TD([makeQuery(id+"F5.opExtrude","SWEPT_FACE",FACE,{"disambiguationData":[OSD([sQuery(id+"F4.wireOp",EDGE,"E46")])]})])],"derivedFrom":makeQuery(id+"F1.opExtrude","CAP_EDGE",EDGE,{"disambiguationData":[OSD([subQ0])],"isStart":true})}),subQ2],"blendedInto":[subQ2]}),subQ3],"blendedInto":[subQ3]}),subQ4],"blendedInto":[subQ4]}),subQ5],"blendedInto":[subQ5]}),subQ5],"blendedInto":[subQ5]});}
            chamfer(context, id + "F22", {"entities" : qUnion([Q0, Q1]), "width" : 5.08 * mm, "tangentPropagation" : true});
        }
        {
            var Q0;
            {var subQ0=sQuery(id+"F0.wireOp",EDGE,"E17");var subQ1=sQuery(id+"F0.wireOp",EDGE,"E16");var subQ2=sQuery(id+"F0.wireOp",EDGE,"E15");var subQ3=sQuery(id+"F0.wireOp",EDGE,"E14");var subQ4=sQuery(id+"F0.wireOp",EDGE,"E13");var subQ5=sQuery(id+"F0.wireOp",EDGE,"E12");var subQ6=sQuery(id+"F0.wireOp",EDGE,"E11");var subQ7=sQuery(id+"F0.wireOp",EDGE,"E8");var subQ8=sQuery(id+"F0.wireOp",EDGE,"E7");var subQ9=sQuery(id+"F0.wireOp",EDGE,"E5");var subQ10=sQuery(id+"F0.wireOp",EDGE,"E4");var subQ11=sQuery(id+"F0.wireOp",EDGE,"E3");var subQ12=sQuery(id+"F0.wireOp",EDGE,"E2");var subQ13=sQuery(id+"F0.wireOp",EDGE,"E0.top");var subQ14=makeQuery(id+"F1.opExtrude","CAP_FACE",FACE,{"disambiguationData":[OSD([subQ13,subQ12,subQ11,subQ10,subQ9,subQ8,subQ7,subQ6,subQ5,subQ4,subQ3,subQ2,subQ1,subQ0])],"isStart":true});var subQ15=subQ14;var subQ16=makeQuery(id+"F7.opChamfer","BLEND_EDGE",EDGE,{"blendedFrom":[makeQuery(id+"F5.boolean.opBoolean","SPLIT",EDGE,{"disambiguationData":[TD([makeQuery(id+"F5.opExtrude","SWEPT_FACE",FACE,{"disambiguationData":[OSD([sQuery(id+"F4.wireOp",EDGE,"E45")])]})])],"derivedFrom":makeQuery(id+"F1.opExtrude","CAP_EDGE",EDGE,{"disambiguationData":[OSD([subQ13])],"isStart":true})}),subQ15],"blendedInto":[subQ15]});var subQ17=subQ15;Q0=makeQuery(id+"F20.opChamfer","BLEND_EDGE",EDGE,{"blendedFrom":[makeQuery(id+"F12.opChamfer","BLEND_EDGE",EDGE,{"blendedFrom":[makeQuery(id+"F11.opChamfer","BLEND_EDGE",EDGE,{"blendedFrom":[subQ16,subQ17],"blendedInto":[subQ17]}),subQ17],"blendedInto":[subQ17]}),makeQuery(id+"F11.opChamfer","BLEND_FACE",FACE,{"disambiguationData":[OSD([subQ13,subQ12,subQ11,subQ10,subQ9,subQ8,subQ7,subQ6,subQ5,subQ4,subQ3,subQ2,subQ1,subQ0]),TDD([subQ16])]})],"blendedInto":[makeQuery(id+"F11.opChamfer","BLEND_FACE",FACE,{"disambiguationData":[OSD([subQ13,subQ12,subQ11,subQ10,subQ9,subQ8,subQ7,subQ6,subQ5,subQ4,subQ3,subQ2,subQ1,subQ0]),TDD([subQ16])]})]});}
            var Q1;
            {var subQ0=sQuery(id+"F0.wireOp",EDGE,"E17");var subQ1=sQuery(id+"F0.wireOp",EDGE,"E16");var subQ2=sQuery(id+"F0.wireOp",EDGE,"E15");var subQ3=sQuery(id+"F0.wireOp",EDGE,"E14");var subQ4=sQuery(id+"F0.wireOp",EDGE,"E13");var subQ5=sQuery(id+"F0.wireOp",EDGE,"E12");var subQ6=sQuery(id+"F0.wireOp",EDGE,"E11");var subQ7=sQuery(id+"F0.wireOp",EDGE,"E8");var subQ8=sQuery(id+"F0.wireOp",EDGE,"E7");var subQ9=sQuery(id+"F0.wireOp",EDGE,"E5");var subQ10=sQuery(id+"F0.wireOp",EDGE,"E4");var subQ11=sQuery(id+"F0.wireOp",EDGE,"E3");var subQ12=sQuery(id+"F0.wireOp",EDGE,"E2");var subQ13=sQuery(id+"F0.wireOp",EDGE,"E0.top");var subQ14=makeQuery(id+"F1.opExtrude","CAP_FACE",FACE,{"disambiguationData":[OSD([subQ13,subQ12,subQ11,subQ10,subQ9,subQ8,subQ7,subQ6,subQ5,subQ4,subQ3,subQ2,subQ1,subQ0])],"isStart":true});var subQ15=subQ14;var subQ16=subQ15;var subQ17=subQ16;var subQ18=makeQuery(id+"F12.opChamfer","BLEND_EDGE",EDGE,{"blendedFrom":[makeQuery(id+"F11.opChamfer","BLEND_EDGE",EDGE,{"blendedFrom":[makeQuery(id+"F7.opChamfer","BLEND_EDGE",EDGE,{"blendedFrom":[makeQuery(id+"F5.boolean.opBoolean","SPLIT",EDGE,{"disambiguationData":[TD([makeQuery(id+"F5.opExtrude","SWEPT_FACE",FACE,{"disambiguationData":[OSD([sQuery(id+"F4.wireOp",EDGE,"E45")])]})])],"derivedFrom":makeQuery(id+"F1.opExtrude","CAP_EDGE",EDGE,{"disambiguationData":[OSD([subQ13])],"isStart":true})}),subQ15],"blendedInto":[subQ15]}),subQ16],"blendedInto":[subQ16]}),subQ17],"blendedInto":[subQ17]});Q1=makeQuery(id+"F21.opChamfer","BLEND_EDGE",EDGE,{"blendedFrom":[makeQuery(id+"F20.opChamfer","BLEND_EDGE",EDGE,{"blendedFrom":[subQ18,subQ17],"blendedInto":[subQ17]}),makeQuery(id+"F20.opChamfer","BLEND_FACE",FACE,{"disambiguationData":[OSD([subQ13,subQ12,subQ11,subQ10,subQ9,subQ8,subQ7,subQ6,subQ5,subQ4,subQ3,subQ2,subQ1,subQ0]),TDD([subQ18])]})],"blendedInto":[makeQuery(id+"F20.opChamfer","BLEND_FACE",FACE,{"disambiguationData":[OSD([subQ13,subQ12,subQ11,subQ10,subQ9,subQ8,subQ7,subQ6,subQ5,subQ4,subQ3,subQ2,subQ1,subQ0]),TDD([subQ18])]})]});}
            var Q2;
            {var subQ0=sQuery(id+"F0.wireOp",EDGE,"E17");var subQ1=sQuery(id+"F0.wireOp",EDGE,"E16");var subQ2=sQuery(id+"F0.wireOp",EDGE,"E15");var subQ3=sQuery(id+"F0.wireOp",EDGE,"E14");var subQ4=sQuery(id+"F0.wireOp",EDGE,"E13");var subQ5=sQuery(id+"F0.wireOp",EDGE,"E12");var subQ6=sQuery(id+"F0.wireOp",EDGE,"E11");var subQ7=sQuery(id+"F0.wireOp",EDGE,"E8");var subQ8=sQuery(id+"F0.wireOp",EDGE,"E7");var subQ9=sQuery(id+"F0.wireOp",EDGE,"E5");var subQ10=sQuery(id+"F0.wireOp",EDGE,"E4");var subQ11=sQuery(id+"F0.wireOp",EDGE,"E3");var subQ12=sQuery(id+"F0.wireOp",EDGE,"E2");var subQ13=sQuery(id+"F0.wireOp",EDGE,"E0.top");var subQ14=makeQuery(id+"F1.opExtrude","CAP_FACE",FACE,{"disambiguationData":[OSD([subQ13,subQ12,subQ11,subQ10,subQ9,subQ8,subQ7,subQ6,subQ5,subQ4,subQ3,subQ2,subQ1,subQ0])],"isStart":true});var subQ15=subQ14;var subQ16=subQ15;var subQ17=subQ16;var subQ18=subQ17;var subQ19=makeQuery(id+"F20.opChamfer","BLEND_EDGE",EDGE,{"blendedFrom":[makeQuery(id+"F12.opChamfer","BLEND_EDGE",EDGE,{"blendedFrom":[makeQuery(id+"F11.opChamfer","BLEND_EDGE",EDGE,{"blendedFrom":[makeQuery(id+"F7.opChamfer","BLEND_EDGE",EDGE,{"blendedFrom":[makeQuery(id+"F5.boolean.opBoolean","SPLIT",EDGE,{"disambiguationData":[TD([makeQuery(id+"F5.opExtrude","SWEPT_FACE",FACE,{"disambiguationData":[OSD([sQuery(id+"F4.wireOp",EDGE,"E45")])]})])],"derivedFrom":makeQuery(id+"F1.opExtrude","CAP_EDGE",EDGE,{"disambiguationData":[OSD([subQ13])],"isStart":true})}),subQ15],"blendedInto":[subQ15]}),subQ16],"blendedInto":[subQ16]}),subQ17],"blendedInto":[subQ17]}),subQ18],"blendedInto":[subQ18]});Q2=makeQuery(id+"F22.opChamfer","BLEND_EDGE",EDGE,{"blendedFrom":[makeQuery(id+"F21.opChamfer","BLEND_EDGE",EDGE,{"blendedFrom":[subQ19,subQ18],"blendedInto":[subQ18]}),makeQuery(id+"F21.opChamfer","BLEND_FACE",FACE,{"disambiguationData":[OSD([subQ13,subQ12,subQ11,subQ10,subQ9,subQ8,subQ7,subQ6,subQ5,subQ4,subQ3,subQ2,subQ1,subQ0]),TDD([subQ19])]})],"blendedInto":[makeQuery(id+"F21.opChamfer","BLEND_FACE",FACE,{"disambiguationData":[OSD([subQ13,subQ12,subQ11,subQ10,subQ9,subQ8,subQ7,subQ6,subQ5,subQ4,subQ3,subQ2,subQ1,subQ0]),TDD([subQ19])]})]});}
            var Q3;
            {var subQ0=sQuery(id+"F0.wireOp",EDGE,"E17");var subQ1=sQuery(id+"F0.wireOp",EDGE,"E16");var subQ2=sQuery(id+"F0.wireOp",EDGE,"E15");var subQ3=sQuery(id+"F0.wireOp",EDGE,"E14");var subQ4=sQuery(id+"F0.wireOp",EDGE,"E13");var subQ5=sQuery(id+"F0.wireOp",EDGE,"E12");var subQ6=sQuery(id+"F0.wireOp",EDGE,"E11");var subQ7=sQuery(id+"F0.wireOp",EDGE,"E8");var subQ8=sQuery(id+"F0.wireOp",EDGE,"E7");var subQ9=sQuery(id+"F0.wireOp",EDGE,"E5");var subQ10=sQuery(id+"F0.wireOp",EDGE,"E4");var subQ11=sQuery(id+"F0.wireOp",EDGE,"E3");var subQ12=sQuery(id+"F0.wireOp",EDGE,"E2");var subQ13=sQuery(id+"F0.wireOp",EDGE,"E0.top");var subQ14=makeQuery(id+"F1.opExtrude","CAP_FACE",FACE,{"disambiguationData":[OSD([subQ13,subQ12,subQ11,subQ10,subQ9,subQ8,subQ7,subQ6,subQ5,subQ4,subQ3,subQ2,subQ1,subQ0])],"isStart":true});var subQ15=subQ14;var subQ16=makeQuery(id+"F7.opChamfer","BLEND_EDGE",EDGE,{"blendedFrom":[makeQuery(id+"F5.boolean.opBoolean","SPLIT",EDGE,{"disambiguationData":[TD([makeQuery(id+"F5.opExtrude","SWEPT_FACE",FACE,{"disambiguationData":[OSD([sQuery(id+"F4.wireOp",EDGE,"E46")])]})])],"derivedFrom":makeQuery(id+"F1.opExtrude","CAP_EDGE",EDGE,{"disambiguationData":[OSD([subQ13])],"isStart":true})}),subQ15],"blendedInto":[subQ15]});var subQ17=subQ15;Q3=makeQuery(id+"F20.opChamfer","BLEND_EDGE",EDGE,{"blendedFrom":[makeQuery(id+"F12.opChamfer","BLEND_EDGE",EDGE,{"blendedFrom":[makeQuery(id+"F11.opChamfer","BLEND_EDGE",EDGE,{"blendedFrom":[subQ16,subQ17],"blendedInto":[subQ17]}),subQ17],"blendedInto":[subQ17]}),makeQuery(id+"F11.opChamfer","BLEND_FACE",FACE,{"disambiguationData":[OSD([subQ13,subQ12,subQ11,subQ10,subQ9,subQ8,subQ7,subQ6,subQ5,subQ4,subQ3,subQ2,subQ1,subQ0]),TDD([subQ16])]})],"blendedInto":[makeQuery(id+"F11.opChamfer","BLEND_FACE",FACE,{"disambiguationData":[OSD([subQ13,subQ12,subQ11,subQ10,subQ9,subQ8,subQ7,subQ6,subQ5,subQ4,subQ3,subQ2,subQ1,subQ0]),TDD([subQ16])]})]});}
            var Q4;
            {var subQ0=sQuery(id+"F0.wireOp",EDGE,"E17");var subQ1=sQuery(id+"F0.wireOp",EDGE,"E16");var subQ2=sQuery(id+"F0.wireOp",EDGE,"E15");var subQ3=sQuery(id+"F0.wireOp",EDGE,"E14");var subQ4=sQuery(id+"F0.wireOp",EDGE,"E13");var subQ5=sQuery(id+"F0.wireOp",EDGE,"E12");var subQ6=sQuery(id+"F0.wireOp",EDGE,"E11");var subQ7=sQuery(id+"F0.wireOp",EDGE,"E8");var subQ8=sQuery(id+"F0.wireOp",EDGE,"E7");var subQ9=sQuery(id+"F0.wireOp",EDGE,"E5");var subQ10=sQuery(id+"F0.wireOp",EDGE,"E4");var subQ11=sQuery(id+"F0.wireOp",EDGE,"E3");var subQ12=sQuery(id+"F0.wireOp",EDGE,"E2");var subQ13=sQuery(id+"F0.wireOp",EDGE,"E0.top");var subQ14=makeQuery(id+"F1.opExtrude","CAP_FACE",FACE,{"disambiguationData":[OSD([subQ13,subQ12,subQ11,subQ10,subQ9,subQ8,subQ7,subQ6,subQ5,subQ4,subQ3,subQ2,subQ1,subQ0])],"isStart":true});var subQ15=subQ14;var subQ16=subQ15;var subQ17=subQ16;var subQ18=makeQuery(id+"F12.opChamfer","BLEND_EDGE",EDGE,{"blendedFrom":[makeQuery(id+"F11.opChamfer","BLEND_EDGE",EDGE,{"blendedFrom":[makeQuery(id+"F7.opChamfer","BLEND_EDGE",EDGE,{"blendedFrom":[makeQuery(id+"F5.boolean.opBoolean","SPLIT",EDGE,{"disambiguationData":[TD([makeQuery(id+"F5.opExtrude","SWEPT_FACE",FACE,{"disambiguationData":[OSD([sQuery(id+"F4.wireOp",EDGE,"E46")])]})])],"derivedFrom":makeQuery(id+"F1.opExtrude","CAP_EDGE",EDGE,{"disambiguationData":[OSD([subQ13])],"isStart":true})}),subQ15],"blendedInto":[subQ15]}),subQ16],"blendedInto":[subQ16]}),subQ17],"blendedInto":[subQ17]});Q4=makeQuery(id+"F21.opChamfer","BLEND_EDGE",EDGE,{"blendedFrom":[makeQuery(id+"F20.opChamfer","BLEND_EDGE",EDGE,{"blendedFrom":[subQ18,subQ17],"blendedInto":[subQ17]}),makeQuery(id+"F20.opChamfer","BLEND_FACE",FACE,{"disambiguationData":[OSD([subQ13,subQ12,subQ11,subQ10,subQ9,subQ8,subQ7,subQ6,subQ5,subQ4,subQ3,subQ2,subQ1,subQ0]),TDD([subQ18])]})],"blendedInto":[makeQuery(id+"F20.opChamfer","BLEND_FACE",FACE,{"disambiguationData":[OSD([subQ13,subQ12,subQ11,subQ10,subQ9,subQ8,subQ7,subQ6,subQ5,subQ4,subQ3,subQ2,subQ1,subQ0]),TDD([subQ18])]})]});}
            var Q5;
            {var subQ0=sQuery(id+"F0.wireOp",EDGE,"E17");var subQ1=sQuery(id+"F0.wireOp",EDGE,"E16");var subQ2=sQuery(id+"F0.wireOp",EDGE,"E15");var subQ3=sQuery(id+"F0.wireOp",EDGE,"E14");var subQ4=sQuery(id+"F0.wireOp",EDGE,"E13");var subQ5=sQuery(id+"F0.wireOp",EDGE,"E12");var subQ6=sQuery(id+"F0.wireOp",EDGE,"E11");var subQ7=sQuery(id+"F0.wireOp",EDGE,"E8");var subQ8=sQuery(id+"F0.wireOp",EDGE,"E7");var subQ9=sQuery(id+"F0.wireOp",EDGE,"E5");var subQ10=sQuery(id+"F0.wireOp",EDGE,"E4");var subQ11=sQuery(id+"F0.wireOp",EDGE,"E3");var subQ12=sQuery(id+"F0.wireOp",EDGE,"E2");var subQ13=sQuery(id+"F0.wireOp",EDGE,"E0.top");var subQ14=makeQuery(id+"F1.opExtrude","CAP_FACE",FACE,{"disambiguationData":[OSD([subQ13,subQ12,subQ11,subQ10,subQ9,subQ8,subQ7,subQ6,subQ5,subQ4,subQ3,subQ2,subQ1,subQ0])],"isStart":true});var subQ15=subQ14;var subQ16=subQ15;var subQ17=subQ16;var subQ18=subQ17;var subQ19=makeQuery(id+"F20.opChamfer","BLEND_EDGE",EDGE,{"blendedFrom":[makeQuery(id+"F12.opChamfer","BLEND_EDGE",EDGE,{"blendedFrom":[makeQuery(id+"F11.opChamfer","BLEND_EDGE",EDGE,{"blendedFrom":[makeQuery(id+"F7.opChamfer","BLEND_EDGE",EDGE,{"blendedFrom":[makeQuery(id+"F5.boolean.opBoolean","SPLIT",EDGE,{"disambiguationData":[TD([makeQuery(id+"F5.opExtrude","SWEPT_FACE",FACE,{"disambiguationData":[OSD([sQuery(id+"F4.wireOp",EDGE,"E46")])]})])],"derivedFrom":makeQuery(id+"F1.opExtrude","CAP_EDGE",EDGE,{"disambiguationData":[OSD([subQ13])],"isStart":true})}),subQ15],"blendedInto":[subQ15]}),subQ16],"blendedInto":[subQ16]}),subQ17],"blendedInto":[subQ17]}),subQ18],"blendedInto":[subQ18]});Q5=makeQuery(id+"F22.opChamfer","BLEND_EDGE",EDGE,{"blendedFrom":[makeQuery(id+"F21.opChamfer","BLEND_EDGE",EDGE,{"blendedFrom":[subQ19,subQ18],"blendedInto":[subQ18]}),makeQuery(id+"F21.opChamfer","BLEND_FACE",FACE,{"disambiguationData":[OSD([subQ13,subQ12,subQ11,subQ10,subQ9,subQ8,subQ7,subQ6,subQ5,subQ4,subQ3,subQ2,subQ1,subQ0]),TDD([subQ19])]})],"blendedInto":[makeQuery(id+"F21.opChamfer","BLEND_FACE",FACE,{"disambiguationData":[OSD([subQ13,subQ12,subQ11,subQ10,subQ9,subQ8,subQ7,subQ6,subQ5,subQ4,subQ3,subQ2,subQ1,subQ0]),TDD([subQ19])]})]});}
            chamfer(context, id + "F23", {"entities" : qUnion([Q0, Q1, Q2, Q3, Q4, Q5]), "width" : 5.08 * mm, "tangentPropagation" : true});
        }
    });
